# Revit family: Golf-IP40-Plain_Door-syst-AT-de
name_source: partatom
category: Electrical Equipment
units: mm (PartAtom-declared; Revit-internal decimal feet)

## family parameters
Cut with Voids When Loaded = No
Host = Face
Panel Configuration = Two Columns, Circuits Across
Part Type = Panelboard
Room Calculation Point = No
Round Connector Dimension = Use Diameter
Shared = No

## types (2) — shared parameters
EF000007 - Farbe = EV000202 - weiß
EF000049 - Tiefe = 98 mm  [stored 0.321522 ft]
EF000116 - RAL-Nummer = 9010
EF000118 - Mit Montageplatte = No
EF000266 - Anzahl der Reihen = 1
EF000339 - Art der Abdeckung = EV004216 - Tür
EF001062 - EMV-Ausführung = No
EF001088 - Anbaumöglichkeit = Yes
EF001131 - Innentiefe = 98 mm  [stored 0.321522 ft]
EF001134 - DIN-Schiene = Yes
EF001596 - Werkstoff des Gehäuses = EV000139 - Kunststoff
EF002950 - Breite in Teilungseinheiten = 22
EF004462 - Art der Schließung = EV000154 - sonstige
EF005474 - Schutzart (IP) = EV006415 - IP40
EF006244 - Transparenter Deckel/Tür = No
EF006306 - Mit Schloss = No
EF009212 - Ausführung Deckel = EV000116 - geschlossen
EF015776 - Erdungsklemmenblock = No
EF015777 - Neutralleiterklemmenblock = No
EF015941 - Signaldurchlassende Tür = No
HG000001 - Anzahl der Spalten = 1
HG000002 - Mit tür = Yes
HG000003 - Bereich = Golf
HG000005 - Dicke = 3 mm  [stored 0.00984252 ft]
HG000009 - Doppelflügeligen Tür = No
HG000010 - Asymmetrische Türen = No
HG000011 - Leere Reihen von unten = No
Manufacturer = Hager
Type Comments = Golf
zero-valued in all types: Default Elevation, HG000007 - Anzahl der leeren Spalten, HG000008 - Anzahl der leeren Reihen

## per-type parameters (varying)
| type | EF000003 - Montageart | EF000008 - Breite | EF000040 - Höhe | EF000218 - Einbautiefe | EF000332 - Einbauhöhe | EF000846 - Einbaubreite | HG000004 - Herstellerreferenz | HG000006 - Unterputz | Model |
| Aufputz IP40 B461.5 H251.5 T98.5 22 Teilungseinheiten - VS122PD | EV000384 - Aufputz | 462 mm | 252 mm | 0 mm  [stored 0 ft] | 0 mm  [stored 0 ft] | 0 mm  [stored 0 ft] | VS122PD | No | VS122PD |
| Unterputz IP40 B532 H293 T97.5 22 Teilungseinheiten - VF122PD | EV000128 - Hohlwand | 532 mm  [stored 1.74541 ft] | 293 mm | 72 mm  [stored 0.23622 ft] | 257 mm  [stored 0.843176 ft] | 498 mm  [stored 1.63386 ft] | VF122PD | Yes | VF122PD |

note: [stored X ft] marks values corroborated as IEEE doubles in the binary element streams (Revit-internal decimal feet)

## geometry (parser evidence)
native form markers: Sweep x12
no freeform markers — native parametric forms only
